# Revit family: Plumbing_Fixtures-Oasis-Drinking_Fountain_OUTDOOR_DGM-BC
name_source: partatom
category: Plumbing Fixtures
units: mm (PartAtom-declared; Revit-internal decimal feet)

## family parameters
Always vertical = No
Cut with Voids When Loaded = No
Maintain Annotation Orientation = No
OmniClass Number = 23.65.70.14.11.11
OmniClass Title = Security Drinking Fountains/Coolers
Part Type = Normal
Room Calculation Point = No
Round Connector Dimension = Use Diameter
Shared = No
Work Plane-Based = No

## types (1)
- PGVMFVBFSL
    Assembly Code = 507604
    CW Connection = Yes
    Default Elevation = 0' - 0"
    Description = OUTDOOR BOTTLE FILLER
    Flow Rate = 8 GPH
    Manufacturer = Oasis International
    Material = Metal, Powder Coated, White
    Model = DGM-BC
    URL = https://www.oasiscoolers.com
    Vent Connection = No
    Waste Connection = Yes
    Water Pressure = 60 PSI (20-100 PSI Range)

## geometry (parser evidence)
native form markers: Sweep x3
no freeform markers — native parametric forms only
